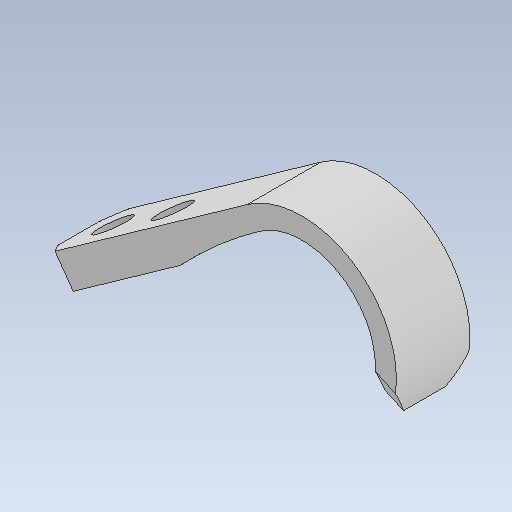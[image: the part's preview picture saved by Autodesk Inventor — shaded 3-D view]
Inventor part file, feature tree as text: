
AUTODESK INVENTOR PART (.ipt)
format: ipt  version: 2020 (Build 240168000, 168)  size: 150,016 bytes
history: native  units: mm
features: reference x4, sketch x3, extrude x3, other x3, chamfer x2, plane x1, projected_geometry x1
ambient origin geometry x8: Origin, YZ Plane, XZ Plane, XY Plane, X Axis, Y Axis, Z Axis, Center Point
bodies: Solid1 (feature_tree)
feature tree (17):
  sketch  "Sketch1"  dims[d0=3.0mm d1=3.0mm]
  plane  "Work Plane1"
  extrude  "Extrusion1"  Depth=3.0mm
  extrude  "Extrusion2"  Depth=18.0mm
  chamfer  "Chamfer1"  Distance=2.0mm
  extrude  "Extrusion3"  Depth=10.0mm
  chamfer  "Chamfer2"  Distance=7.0mm
  reference  "Reference1"
  reference  "Reference2"
  sketch  "Sketch2"  dims[d2=24.0mm d3=18.0mm]
  reference  "Reference3"
  reference  "Reference4"
  sketch  "Sketch3"  dims[d4=9.0mm d5=2.0mm d6=14.0mm d7=7.0mm d8=10.0mm d9=0.0mm d10=3.2mm d11=3.2mm d12=10.0mm d13=0.0mm d14=1.5mm d15=2.0mm d16=45.0deg d17=30.0deg d18=10.0mm d19=0.0mm d20=1.5mm d21=2.0mm d22=60.0deg]
  projected_geometry  "Projected Loop1"
  parser-record x1  (decoder bookkeeping rows leaked as tree rows — omitted from the tree; the rows remain in map.json)
  other  "leg_1.iam"
  other  "leg_link_1:1"
note: 1 file-system path scrubbed to <path> (originals preserved in map.json)
